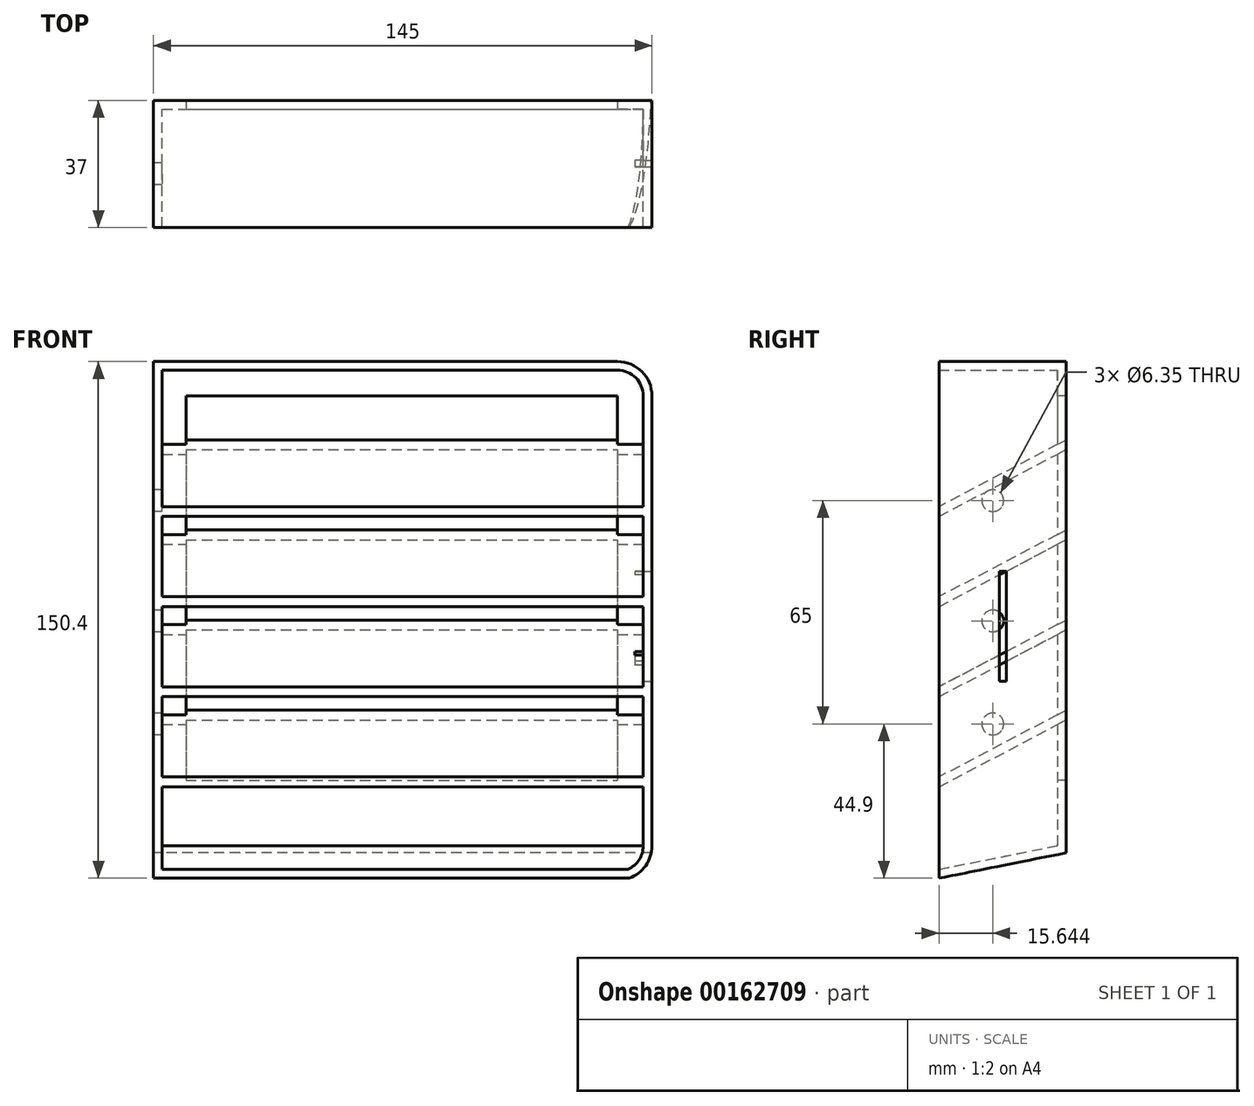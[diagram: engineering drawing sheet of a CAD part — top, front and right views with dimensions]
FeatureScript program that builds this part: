
annotation { "Feature Type Name" : "Feature", "Feature Type Description" : "" }
export const myFeature = defineFeature(function(context is Context, id is Id, definition is map)
    precondition{}
    {
        {
            var Q0;
            Q0=qCreatedBy(makeId("Front.planeOp"),FACE);
            var sketch = newSketch(context, id + "F0", { "sketchPlane" : qUnion([Q0])});
            skLineSegment(sketch, "E0.bottom", {"start": v(-72.5, 75.5) * mm, "end": v(62.5, 75.5) * mm});
            skLineSegment(sketch, "E0.top", {"start": v(-72.5, -75.5) * mm, "end": v(62.5, -75.5) * mm});
            skLineSegment(sketch, "E0.left", {"start": v(-72.5, 75.5) * mm, "end": v(-72.5, -75.5) * mm});
            skLineSegment(sketch, "E0.right", {"start": v(72.5, 65.5) * mm, "end": v(72.5, -65.5) * mm});
            skPoint(sketch, "E0.middle", {"position": v(0, 0) * mm});
            skPoint(sketch, "E1.visualSharp", {"position": v(72.5, 75.5) * mm});
            skArc(sketch, "E1.filletArc", {"start": v(72.5, 65.5) * mm, "mid": v(69.57, 72.57) * mm, "end": v(62.5, 75.5) * mm});
            skPoint(sketch, "E2.visualSharp", {"position": v(72.5, -75.5) * mm});
            skArc(sketch, "E2.filletArc", {"start": v(62.5, -75.5) * mm, "mid": v(69.57, -72.57) * mm, "end": v(72.5, -65.5) * mm});
            skSolve(sketch);
        }
        {
            var Q0;
            Q0 = qSketchRegion(id + "F0", true);
            extrude(context, id + "F1", {"entities" : qUnion([Q0]), "depth" : 37 * mm});
        }
        {
            var Q0;
            Q0=makeQuery(id+"F1.opExtrude","CAP_EDGE",EDGE,{"disambiguationData":[OSD([sQuery(id+"F0.wireOp",EDGE,"E0.top")])],"isStart":true});
            chamfer(context, id + "F2", {"entities" : qUnion([Q0]), "chamferType" : ChamferType.TWO_OFFSETS, "width1" : 40 * mm, "oppositeDirection" : false, "width2" : 8 * mm});
        }
        {
            var Q0;
            Q0=makeQuery(id+"F1.opExtrude","CAP_FACE",FACE,{"disambiguationData":[OSD([sQuery(id+"F0.wireOp",EDGE,"E0.bottom"),sQuery(id+"F0.wireOp",EDGE,"E0.top"),sQuery(id+"F0.wireOp",EDGE,"E0.left"),sQuery(id+"F0.wireOp",EDGE,"E0.right"),sQuery(id+"F0.wireOp",EDGE,"E1.filletArc"),sQuery(id+"F0.wireOp",EDGE,"E2.filletArc")])],"isStart":false});
            shell(context, id + "F3", {"entities" : qUnion([Q0]), "thickness" : 2.54 * mm});
        }
        {
            var Q0;
            Q0=makeQuery(id+"F3.opShell","OFFSET_FACE",FACE,{"disambiguationData":[OSD([sQuery(id+"F0.wireOp",EDGE,"E0.bottom"),sQuery(id+"F0.wireOp",EDGE,"E0.top"),sQuery(id+"F0.wireOp",EDGE,"E0.left"),sQuery(id+"F0.wireOp",EDGE,"E0.right"),sQuery(id+"F0.wireOp",EDGE,"E1.filletArc"),sQuery(id+"F0.wireOp",EDGE,"E2.filletArc")])]});
            var sketch = newSketch(context, id + "F4", { "sketchPlane" : qUnion([Q0])});
            skPoint(sketch, "E3.middle", {"position": v(0, 0) * mm});
            skLineSegment(sketch, "E4.bottom", {"start": v(-63.05, 65.5) * mm, "end": v(62.5, 65.5) * mm});
            skLineSegment(sketch, "E4.top", {"start": v(-63.05, -46.42) * mm, "end": v(62.5, -46.42) * mm});
            skLineSegment(sketch, "E4.left", {"start": v(-63.05, 65.5) * mm, "end": v(-63.05, -46.42) * mm});
            skLineSegment(sketch, "E4.right", {"start": v(62.5, 65.5) * mm, "end": v(62.5, -46.42) * mm});
            skSolve(sketch);
        }
        {
            var Q0;
            Q0=makeQuery(id+"F4.imprint","IMPRINT",FACE,{"disambiguationData":[TD([[makeQuery(id+"F4.imprint","IMPRINT",EDGE,{"derivedFrom":sQuery(id+"F4.wireOp",EDGE,"E4.bottom")}),-1.0]])]});
            extrude(context, id + "F5", {"entities" : qUnion([Q0]), "operationType" : NewBodyOperationType.REMOVE, "oppositeDirection" : true, "depth" : 25.4 * mm});
        }
        {
            var Q0;
            Q0=makeQuery(id+"F1.opExtrude","SWEPT_FACE",FACE,{"disambiguationData":[OSD([sQuery(id+"F0.wireOp",EDGE,"E0.left")])]});
            var sketch = newSketch(context, id + "F6", { "sketchPlane" : qUnion([Q0])});
            skLineSegment(sketch, "E5.0.0", {"start": v(0, -65.5) * mm, "end": v(0, 65.5) * mm});
            skLineSegment(sketch, "E5.0.1", {"start": v(0, 65.5) * mm, "end": v(37, 65.5) * mm});
            skLineSegment(sketch, "E5.0.2", {"start": v(37, 65.5) * mm, "end": v(37, -65.5) * mm});
            skLineSegment(sketch, "E5.0.3", {"start": v(37, -65.5) * mm, "end": v(0, -65.5) * mm});
            skLineSegment(sketch, "E6.0.0", {"start": v(0, 75.5) * mm, "end": v(0, -67.5) * mm});
            skLineSegment(sketch, "E6.0.1", {"start": v(0, -67.5) * mm, "end": v(37, -74.9) * mm});
            skLineSegment(sketch, "E6.0.2", {"start": v(37, -74.9) * mm, "end": v(37, 75.5) * mm});
            skLineSegment(sketch, "E6.0.3", {"start": v(37, 75.5) * mm, "end": v(0, 75.5) * mm});
            skCircle(sketch, "E7", {"center": v(21.36, 0) * mm, "radius": 3.18 * mm});
            skCircle(sketch, "E8.0.1.0", {"center": v(21.36, -30) * mm, "radius": 3.18 * mm});
            skLineSegment(sketch, "E8.direction2", {"start": v(21.36, 0) * mm, "end": v(21.36, -30) * mm, "construction": true});
            skCircle(sketch, "E9", {"center": v(21.36, 35) * mm, "radius": 3.18 * mm});
            skSolve(sketch);
        }
        {
            var Q0;
            Q0=makeQuery(id+"F6.imprint","IMPRINT",FACE,{"disambiguationData":[TD([[makeQuery(id+"F6.imprint","IMPRINT",EDGE,{"derivedFrom":sQuery(id+"F6.wireOp",EDGE,"E7")}),1.0]])]});
            var Q1;
            Q1=makeQuery(id+"F6.imprint","IMPRINT",FACE,{"disambiguationData":[TD([[makeQuery(id+"F6.imprint","IMPRINT",EDGE,{"derivedFrom":sQuery(id+"F6.wireOp",EDGE,"E9")}),1.0]])]});
            var Q2;
            Q2=makeQuery(id+"F6.imprint","IMPRINT",FACE,{"disambiguationData":[TD([[makeQuery(id+"F6.imprint","IMPRINT",EDGE,{"derivedFrom":sQuery(id+"F6.wireOp",EDGE,"E8.0.1.0")}),1.0]])]});
            var Q3;
            Q3=sQuery(id+"F6.wireOp",EDGE,"E9");
            var Q4;
            Q4=sQuery(id+"F6.wireOp",EDGE,"E7");
            var Q5;
            Q5=sQuery(id+"F6.wireOp",EDGE,"E8.0.1.0");
            extrude(context, id + "F7", {"entities" : qUnion([Q0, Q1, Q2]), "operationType" : NewBodyOperationType.REMOVE, "surfaceEntities" : qUnion([Q3, Q4, Q5]), "oppositeDirection" : true, "depth" : 19.05 * mm});
        }
        {
            var Q0;
            Q0=makeQuery(id+"F3.opShell","OFFSET_FACE",FACE,{"disambiguationData":[OSD([sQuery(id+"F0.wireOp",EDGE,"E0.right")])]});
            var sketch = newSketch(context, id + "F8", { "sketchPlane" : qUnion([Q0])});
            skLineSegment(sketch, "E10", {"start": v(37, -48.29) * mm, "end": v(0, -28.87) * mm});
            skLineSegment(sketch, "E11", {"start": v(0, -28.87) * mm, "end": v(0, -26) * mm});
            skLineSegment(sketch, "E12", {"start": v(0, -26) * mm, "end": v(37, -45.42) * mm});
            skLineSegment(sketch, "E13", {"start": v(37, -45.42) * mm, "end": v(37, -48.29) * mm});
            skLineSegment(sketch, "E14", {"start": v(37, -22.05) * mm, "end": v(0, -2.64) * mm});
            skLineSegment(sketch, "E15", {"start": v(0, -2.64) * mm, "end": v(0, 0.23) * mm});
            skLineSegment(sketch, "E16", {"start": v(0, 0.23) * mm, "end": v(37, -19.18) * mm});
            skLineSegment(sketch, "E17", {"start": v(37, -19.18) * mm, "end": v(37, -22.05) * mm});
            skLineSegment(sketch, "E18", {"start": v(37, 4.18) * mm, "end": v(0, 23.6) * mm});
            skLineSegment(sketch, "E19", {"start": v(0, 23.6) * mm, "end": v(0, 26.47) * mm});
            skLineSegment(sketch, "E20", {"start": v(0, 26.47) * mm, "end": v(37, 7.05) * mm});
            skLineSegment(sketch, "E21", {"start": v(37, 7.05) * mm, "end": v(37, 4.18) * mm});
            skLineSegment(sketch, "E22", {"start": v(37, 30.42) * mm, "end": v(0, 49.84) * mm});
            skLineSegment(sketch, "E23", {"start": v(0, 49.84) * mm, "end": v(0, 52.7) * mm});
            skLineSegment(sketch, "E24", {"start": v(0, 52.7) * mm, "end": v(37, 33.29) * mm});
            skLineSegment(sketch, "E25", {"start": v(37, 33.29) * mm, "end": v(37, 30.42) * mm});
            skSolve(sketch);
        }
        {
            var Q0;
            Q0 = qSketchRegion(id + "F8", true);
            extrude(context, id + "F9", {"entities" : qUnion([Q0]), "operationType" : NewBodyOperationType.ADD, "depth" : 142.24 * mm});
        }
        {
            var Q0;
            Q0=makeQuery(id+"F1.opExtrude","SWEPT_FACE",FACE,{"disambiguationData":[OSD([sQuery(id+"F0.wireOp",EDGE,"E0.right")])]});
            var sketch = newSketch(context, id + "F10", { "sketchPlane" : qUnion([Q0])});
            skLineSegment(sketch, "E26.bottom", {"start": v(-19.4, 14.45) * mm, "end": v(-17.4, 14.45) * mm});
            skLineSegment(sketch, "E26.top", {"start": v(-19.4, -17.55) * mm, "end": v(-17.4, -17.55) * mm});
            skLineSegment(sketch, "E26.left", {"start": v(-19.4, 14.45) * mm, "end": v(-19.4, -17.55) * mm});
            skLineSegment(sketch, "E26.right", {"start": v(-17.4, 14.45) * mm, "end": v(-17.4, -17.55) * mm});
            skPoint(sketch, "E26.middle", {"position": v(-17.56, 0) * mm});
            skLineSegment(sketch, "E27.bottom", {"start": v(-37, 75.55) * mm, "end": v(0, 75.55) * mm});
            skLineSegment(sketch, "E27.top", {"start": v(-37, -74.92) * mm, "end": v(0, -74.92) * mm});
            skLineSegment(sketch, "E27.left", {"start": v(-37, 75.55) * mm, "end": v(-37, -74.92) * mm});
            skLineSegment(sketch, "E27.right", {"start": v(0, 75.55) * mm, "end": v(0, -74.92) * mm});
            skSolve(sketch);
        }
        {
            var Q0;
            Q0=makeQuery(id+"F10.imprint","IMPRINT",FACE,{"disambiguationData":[TD([[makeQuery(id+"F10.imprint","IMPRINT",EDGE,{"derivedFrom":sQuery(id+"F10.wireOp",EDGE,"E26.bottom")}),-1.0]])]});
            var Q1;
            Q1=sQuery(id+"F10.wireOp",EDGE,"E26.right");
            var Q2;
            Q2=sQuery(id+"F10.wireOp",EDGE,"E26.bottom");
            var Q3;
            Q3=sQuery(id+"F10.wireOp",EDGE,"E26.left");
            var Q4;
            Q4=sQuery(id+"F10.wireOp",EDGE,"E26.top");
            extrude(context, id + "F11", {"entities" : qUnion([Q0]), "operationType" : NewBodyOperationType.REMOVE, "surfaceEntities" : qUnion([Q1, Q2, Q3, Q4]), "oppositeDirection" : true, "depth" : 5 * mm});
        }
    });
